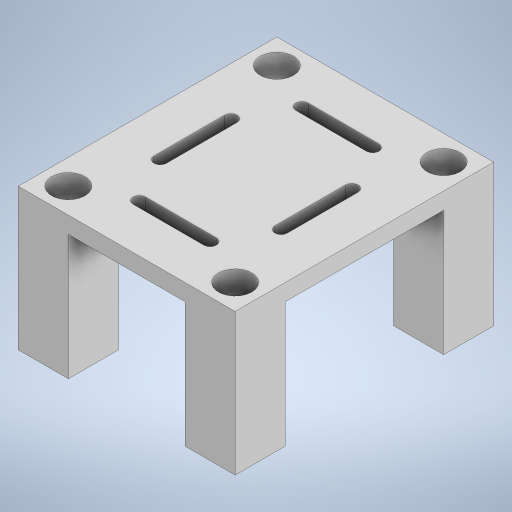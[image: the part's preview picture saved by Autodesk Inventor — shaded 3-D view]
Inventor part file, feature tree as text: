
AUTODESK INVENTOR PART (.ipt)
format: ipt  version: 2023 (Build 270158000, 158)  size: 709,120 bytes
history: native  units: mm
features: extrude x5, sketch x5, other x1
ambient origin geometry x8: Origin, YZ Plane, XZ Plane, XY Plane, X Axis, Y Axis, Z Axis, Center Point
bodies: Body1 (feature_tree)
feature tree (11):
  other  "Bryła1"
  extrude  "Wyciągnięcie proste1"  Depth=50.0mm
  extrude  "Wyciągnięcie proste2"  Depth=40.0mm
  extrude  "Wyciągnięcie proste3"  Depth=12.0mm
  extrude  "Wyciągnięcie proste4"  Depth=12.0mm
  extrude  "Wyciągnięcie proste5"  Depth=12.0mm
  sketch  "Szkic1"
  sketch  "Szkic2"
  sketch  "Szkic3"
  sketch  "Szkic4"
  sketch  "Szkic5"
